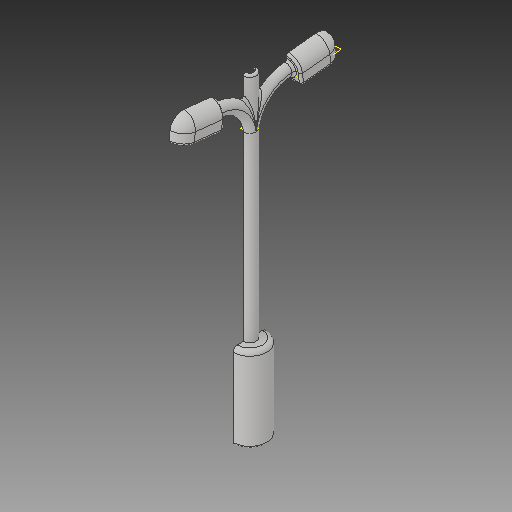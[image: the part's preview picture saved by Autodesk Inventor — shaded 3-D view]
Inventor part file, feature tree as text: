
AUTODESK INVENTOR PART (.ipt)
format: ipt  version: 2018 (Build 220112000, 112)  size: 401,408 bytes
history: native  units: in
note: dims shown in document units (in); Inventor stores cm internally (conversion verified against a paired STEP export)
features: sketch x11, other x3, plane x1
ambient origin geometry x8: Origin, YZ Plane, XZ Plane, XY Plane, X Axis, Y Axis, Z Axis, Center Point
bodies: Solid1 (feature_tree)
feature tree (15):
  other  "lampa_dual.ipt"
  other  "Solid1::lampa_dual.ipt"
  other  "TaggingFeature1"
  sketch  "Sketch1"  dims[d0=0.3937in]
  sketch  "Sketch6"
  sketch  "Sketch8"
  sketch  "Sketch9"
  sketch  "Sketch10"
  sketch  "Sketch11"
  sketch  "Sketch12"
  sketch  "Sketch13"
  sketch  "Sketch14"
  sketch  "Sketch15"
  sketch  "Sketch16"
  plane  "Work Plane1"
